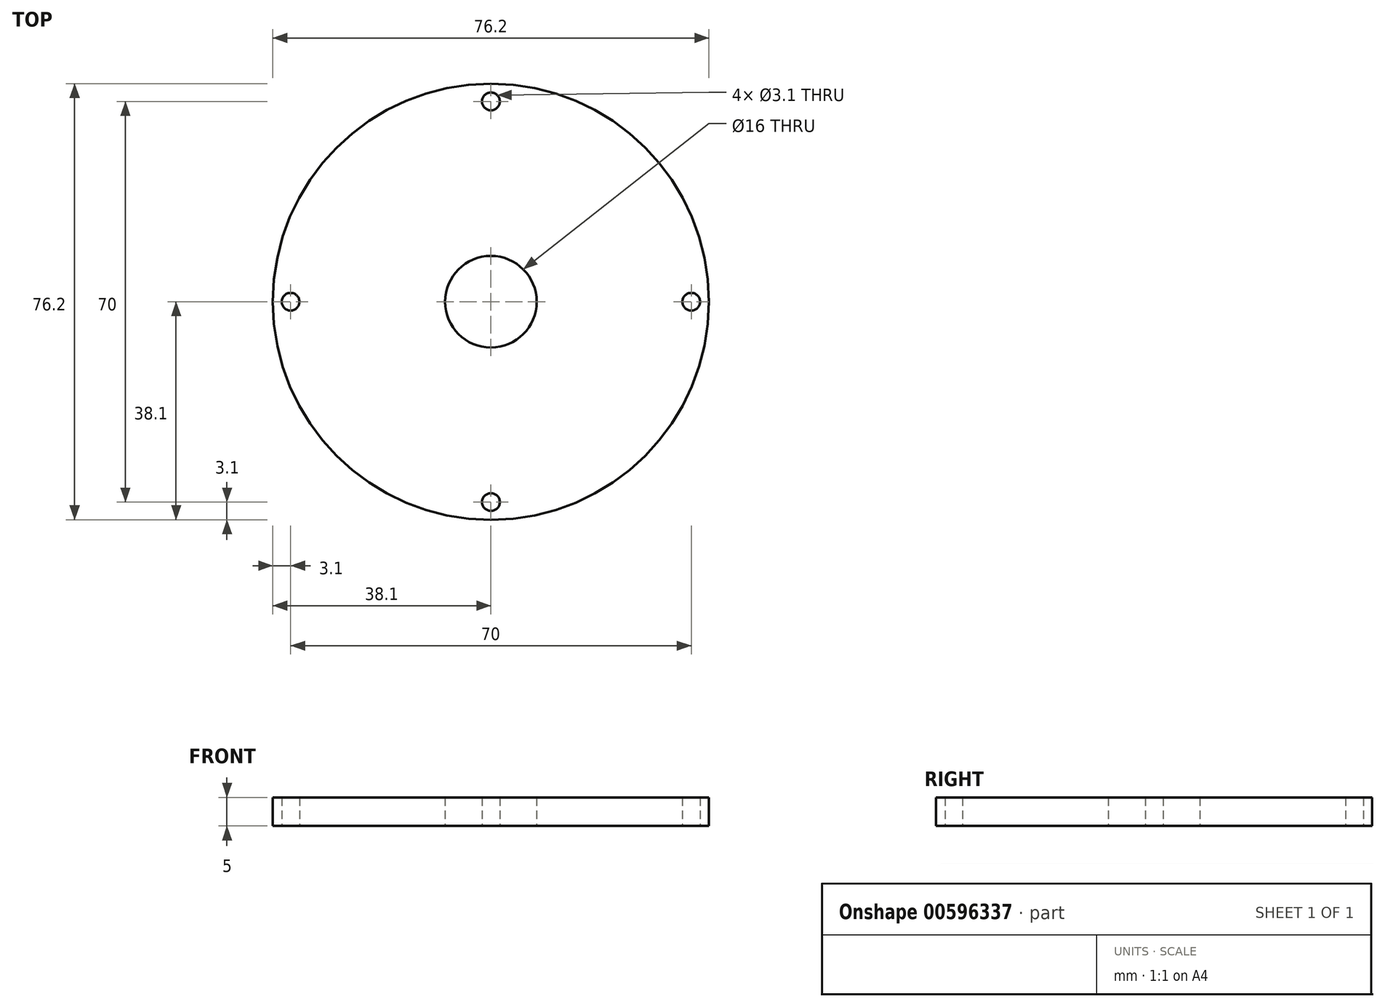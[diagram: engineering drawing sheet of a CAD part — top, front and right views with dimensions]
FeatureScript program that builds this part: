
annotation { "Feature Type Name" : "Feature", "Feature Type Description" : "" }
export const myFeature = defineFeature(function(context is Context, id is Id, definition is map)
    precondition{}
    {
        {
            var Q0;
            Q0=qCreatedBy(makeId("Top.planeOp"),FACE);
            var sketch = newSketch(context, id + "F0", { "sketchPlane" : qUnion([Q0])});
            skCircle(sketch, "E0", {"center": v(0, 0) * mm, "radius": 38.1 * mm});
            skCircle(sketch, "E1", {"center": v(0, 0) * mm, "radius": 8 * mm});
            skCircle(sketch, "E2", {"center": v(0, 35) * mm, "radius": 1.55 * mm});
            skSolve(sketch);
        }
        {
            var Q0;
            Q0=makeQuery(id+"F0.imprint","IMPRINT",FACE,{"disambiguationData":[TD([[makeQuery(id+"F0.imprint","IMPRINT",EDGE,{"derivedFrom":sQuery(id+"F0.wireOp",EDGE,"E0")}),1.0]])]});
            var Q1;
            Q1=makeQuery(id+"F0.imprint","IMPRINT",FACE,{"disambiguationData":[TD([[makeQuery(id+"F0.imprint","IMPRINT",EDGE,{"derivedFrom":sQuery(id+"F0.wireOp",EDGE,"E2")}),1.0]])]});
            extrude(context, id + "F1", {"entities" : qUnion([Q0, Q1]), "depth" : 5 * mm, "offsetDistance" : 25 * mm});
        }
        {
            var Q0;
            Q0=makeQuery(id+"F0.imprint","IMPRINT",FACE,{"disambiguationData":[TD([[makeQuery(id+"F0.imprint","IMPRINT",EDGE,{"derivedFrom":sQuery(id+"F0.wireOp",EDGE,"E2")}),1.0]])]});
            extrude(context, id + "F2", {"entities" : qUnion([Q0]), "depth" : 25 * mm, "offsetDistance" : 25 * mm});
        }
        {
            var Q0;
            Q0=makeQuery(id+"F2.opExtrude","SWEPT_BODY",BODY,{"disambiguationData":[OSD([sQuery(id+"F0.wireOp",EDGE,"E2")])]});
            var Q1;
            Q1=sQuery(id+"F0.wireOp",EDGE,"E0");
            circularPattern(context, id + "F3", {"operationType" : NewBodyOperationType.REMOVE, "entities" : qUnion([Q0]), "axis" : qUnion([Q1]), "angle" : 360 * degree, "instanceCount" : 4, "equalSpace" : true});
        }
    });
